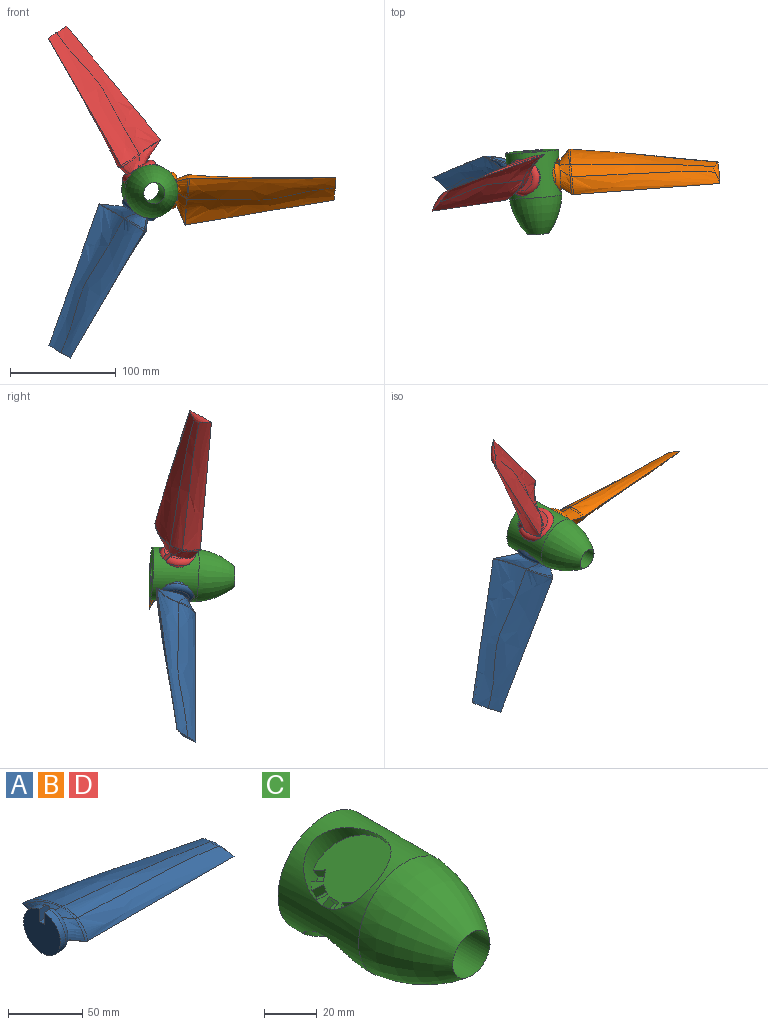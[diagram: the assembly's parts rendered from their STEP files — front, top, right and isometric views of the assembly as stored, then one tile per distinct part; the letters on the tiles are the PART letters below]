
ASSEMBLY  parts=4 mates=1
PART A: 31 faces, bbox 165.4x75.5x38.2 mm
  f0: plane 9.48x8.65mm, normal (1,0,0), area 28.5mm2, adj f11,f16,f21,f30
  f1: plane 22.9x10.19mm, normal (1,0,0), area 88.6mm2, adj f14,f15,f30
  f2: plane 9.2x7.84mm, normal (1,0,0), area 30.8mm2, adj f11,f12,f13,f20,f30
  f3: bspline ~140x50.01mm, area 3008.1mm2, adj f5,f6,f8,f10,f14,f23,f24,f27
  f4: bspline ~140x44.79mm, area 3177.1mm2, adj f5,f9,f10,f28,f29
  f5: bspline ~46.76x8.29mm, area 139.2mm2, adj f3,f4,f6,f7,f8,f9,f10
  f6: plane 3.68x0.3mm, normal (1,0,0), area 0.3mm2, adj f3,f5,f8
  f7: bspline ~140x14.27mm, area 2106.1mm2, adj f5,f8,f9,f25
  f8: bspline ~140x31.34mm, area 3409.3mm2, adj f3,f5,f6,f7,f24,f25
  f9: bspline ~134.76x13.88mm, area 1513.5mm2, adj f4,f5,f7,f25,f26
  f10: bspline ~146.74x35.65mm, area 378.7mm2, adj f3,f4,f5,f29
  f11: bspline ~16.56x9.38mm, area 97.8mm2, adj f0,f2,f12,f16,f19,f25,f26,f28
  f12: bspline ~36.99x15.08mm, area 217.7mm2, adj f2,f11,f13,f29
  f13: bspline ~30.31x12.09mm, area 57.8mm2, adj f2,f12,f14,f29,f30
  f14: bspline ~45.48x10.64mm, area 306.5mm2, adj f1,f3,f13,f15,f23,f24,f27,f29
  f15: bspline ~27.91x10.97mm, area 189.3mm2, adj f1,f14,f16,f24,f25,f30
  f16: bspline ~20.44x14.51mm, area 183.2mm2, adj f0,f11,f15,f25,f30
  f17: cylinder r=17.5mm len=35mm, axis (1,0,0), area 524.7mm2, adj f18,f20,f21,f30
  f18: plane 35x34.82mm, normal (-1,0,0), area 911.5mm2, adj f17,f20,f21,f22
  f19: plane 5x0.7mm, normal (-1,0,0), area 3mm2, adj f11,f20,f21,f22
  f20: plane 10.5x10.5mm, normal (0,-1,0), area 94.6mm2, adj f2,f17,f18,f19,f22,f30
  f21: plane 10.5x10.5mm, normal (0,1,0), area 94.6mm2, adj f0,f17,f18,f19,f22,f30
  f22: plane 10x5mm, normal (0,0,1), area 50mm2, adj f18,f19,f20,f21
  f23: bspline ~6.58x1.92mm, area 2.5mm2, adj f3,f14,f24
  f24: bspline ~28.34x3.32mm, area 39.4mm2, adj f3,f8,f14,f15,f23,f25
  f25: bspline ~15.48x11.23mm, area 36.8mm2, adj f7,f8,f9,f11,f15,f16,f24,f26
  f26: bspline ~14.26x3.07mm, area 21.6mm2, adj f9,f11,f25,f28
  f27: bspline ~28.01x2.7mm, area 15.1mm2, adj f3,f14,f29
  f28: bspline ~2.81x1.55mm, area 0.3mm2, adj f4,f11,f26,f29
  f29: bspline ~39.22x17.45mm, area 88mm2, adj f3,f4,f10,f11,f12,f13,f14,f27
  f30: torus R=12.5mm, axis (-1,0,0), area 704.3mm2, adj f0,f1,f2,f13,f14,f15,f16,f17
PART B: same geometry as A
PART C: 70 faces, bbox 52.7x78.6x60.8 mm
  f0: plane 35x30.16mm, normal (-0.5,0,0.87), area 832.3mm2, adj f8,f49,f50,f51,f53,f54,f55,f57
  f1: plane 35x30.16mm, normal (-0.5,0,-0.87), area 832.3mm2, adj f7,f29,f30,f31,f33,f34,f35,f37
  f2: plane 35x34.82mm, normal (1,0,0), area 832.3mm2, adj f6,f9,f10,f11,f13,f14,f15,f17
  f3: cylinder r=25mm len=50mm, axis (0,1,0), area 3675.1mm2, adj f4,f5,f6,f7,f8
  f4: revolved ~50x50mm, area 9429.9mm2, adj f3,f69
  f5: plane 50x50mm, normal (0,1,0), area 1649.3mm2, adj f3,f69
  f6: cylinder r=17.5mm len=35mm, axis (1,0,0), area 848.2mm2, adj f2,f3,f9,f11,f12,f13,f15,f16
  f7: cylinder r=17.5mm len=37.81mm, axis (-0.5,0,-0.87), area 848.2mm2, adj f1,f3,f29,f31,f32,f33,f35,f36
  f8: cylinder r=17.5mm len=37.81mm, axis (-0.5,0,0.87), area 848.5mm2, adj f0,f3,f49,f51,f52,f53,f55,f56
  f9: plane 5.07x5mm, normal (0,1,0), area 25.4mm2, adj f2,f6,f10,f12
  f10: plane 5x5mm, normal (0,0,1), area 25mm2, adj f2,f9,f11,f12
  f11: plane 5.07x5mm, normal (0,-1,0), area 25.4mm2, adj f2,f6,f10,f12
  f12: plane 5.25x5mm, normal (1,0,0), area 26mm2, adj f6,f9,f10,f11
  f13: plane 5x4.39mm, normal (0,0.5,0.87), area 25.4mm2, adj f2,f6,f14,f16
  f14: plane 5x4.33mm, normal (0,-0.87,0.5), area 25mm2, adj f2,f13,f15,f16
  f15: plane 5x4.39mm, normal (0,-0.5,-0.87), area 25.4mm2, adj f2,f6,f14,f16
  f16: plane 6.89x6.87mm, normal (1,0,0), area 26mm2, adj f6,f13,f14,f15
  f17: plane 5x4.39mm, normal (0,0.87,0.5), area 25.4mm2, adj f2,f6,f18,f20
  f18: plane 5x4.33mm, normal (0,-0.5,0.87), area 25mm2, adj f2,f17,f19,f20
  f19: plane 5x4.39mm, normal (0,-0.87,-0.5), area 25.4mm2, adj f2,f6,f18,f20
  f20: plane 6.89x6.87mm, normal (1,0,0), area 26mm2, adj f6,f17,f18,f19
  f21: plane 5x4.39mm, normal (0,0.5,-0.87), area 25.4mm2, adj f2,f6,f22,f24
  f22: plane 5x4.33mm, normal (0,0.87,0.5), area 25mm2, adj f2,f21,f23,f24
  f23: plane 5x4.39mm, normal (0,-0.5,0.87), area 25.4mm2, adj f2,f6,f22,f24
  f24: plane 6.89x6.87mm, normal (1,0,0), area 26mm2, adj f6,f21,f22,f23
  f25: plane 5x4.39mm, normal (0,0.87,-0.5), area 25.4mm2, adj f2,f6,f26,f28
  f26: plane 5x4.33mm, normal (0,0.5,0.87), area 25mm2, adj f2,f25,f27,f28
  f27: plane 5x4.39mm, normal (0,-0.87,0.5), area 25.4mm2, adj f2,f6,f26,f28
  f28: plane 6.89x6.87mm, normal (1,0,0), area 26mm2, adj f6,f25,f26,f27
  f29: plane 6.89x6.87mm, normal (0,1,0), area 25.4mm2, adj f1,f7,f30,f32
  f30: plane 5x4.33mm, normal (0.87,0,-0.5), area 25mm2, adj f1,f29,f31,f32
  f31: plane 6.89x6.87mm, normal (0,-1,0), area 25.4mm2, adj f1,f7,f30,f32
  f32: plane 5x4.55mm, normal (-0.5,0,-0.87), area 26mm2, adj f7,f29,f30,f31
  f33: plane 5.6x4.7mm, normal (0.75,0.5,-0.43), area 25.4mm2, adj f1,f7,f34,f36
  f34: plane 6.5x6.25mm, normal (0.43,-0.87,-0.25), area 25mm2, adj f1,f33,f35,f36
  f35: plane 5.6x4.7mm, normal (-0.75,-0.5,0.43), area 25.4mm2, adj f1,f7,f34,f36
  f36: plane 6.89x5.95mm, normal (-0.5,0,-0.87), area 26mm2, adj f7,f33,f34,f35
  f37: plane 6.53x6.3mm, normal (0.43,0.87,-0.25), area 25.4mm2, adj f1,f7,f38,f40
  f38: plane 5.58x4.67mm, normal (0.75,-0.5,-0.43), area 25mm2, adj f1,f37,f39,f40
  f39: plane 6.53x6.3mm, normal (-0.43,-0.87,0.25), area 25.4mm2, adj f1,f7,f38,f40
  f40: plane 6.87x5.97mm, normal (-0.5,0,-0.87), area 26mm2, adj f7,f37,f38,f39
  f41: plane 5.6x4.7mm, normal (-0.75,0.5,0.43), area 25.4mm2, adj f1,f7,f42,f44
  f42: plane 6.5x6.25mm, normal (0.43,0.87,-0.25), area 25mm2, adj f1,f41,f43,f44
  f43: plane 5.6x4.7mm, normal (0.75,-0.5,-0.43), area 25.4mm2, adj f1,f7,f42,f44
  f44: plane 6.89x5.95mm, normal (-0.5,0,-0.87), area 26mm2, adj f7,f41,f42,f43
  f45: plane 6.53x6.3mm, normal (-0.43,0.87,0.25), area 25.4mm2, adj f1,f7,f46,f48
  f46: plane 5.58x4.67mm, normal (0.75,0.5,-0.43), area 25mm2, adj f1,f45,f47,f48
  f47: plane 6.53x6.3mm, normal (0.43,-0.87,-0.25), area 25.4mm2, adj f1,f7,f46,f48
  f48: plane 6.87x5.97mm, normal (-0.5,0,-0.87), area 26mm2, adj f7,f45,f46,f47
  f49: plane 6.89x6.87mm, normal (0,1,0), area 25.4mm2, adj f0,f8,f50,f52
  f50: plane 5x4.33mm, normal (-0.87,0,-0.5), area 25mm2, adj f0,f49,f51,f52
  f51: plane 6.89x6.87mm, normal (0,-1,0), area 25.4mm2, adj f0,f8,f50,f52
  f52: plane 5x4.55mm, normal (-0.5,0,0.87), area 26mm2, adj f8,f49,f50,f51
  f53: plane 5.6x4.7mm, normal (-0.75,0.5,-0.43), area 25.4mm2, adj f0,f8,f54,f56
  f54: plane 6.5x6.25mm, normal (-0.43,-0.87,-0.25), area 25mm2, adj f0,f53,f55,f56
  f55: plane 5.6x4.7mm, normal (0.75,-0.5,0.43), area 25.4mm2, adj f0,f8,f54,f56
  f56: plane 6.89x5.95mm, normal (-0.5,0,0.87), area 26mm2, adj f8,f53,f54,f55
  f57: plane 6.53x6.3mm, normal (-0.43,0.87,-0.25), area 25.4mm2, adj f0,f8,f58,f60
  f58: plane 5.58x4.67mm, normal (-0.75,-0.5,-0.43), area 25mm2, adj f0,f57,f59,f60
  f59: plane 6.53x6.3mm, normal (0.43,-0.87,0.25), area 25.4mm2, adj f0,f8,f58,f60
  f60: plane 6.87x5.97mm, normal (-0.5,0,0.87), area 26mm2, adj f8,f57,f58,f59
  f61: plane 5.6x4.7mm, normal (0.75,0.5,0.43), area 25.4mm2, adj f0,f8,f62,f64
  f62: plane 6.5x6.25mm, normal (-0.43,0.87,-0.25), area 25mm2, adj f0,f61,f63,f64
  f63: plane 5.6x4.7mm, normal (-0.75,-0.5,-0.43), area 25.4mm2, adj f0,f8,f62,f64
  f64: plane 6.89x5.95mm, normal (-0.5,0,0.87), area 26mm2, adj f8,f61,f62,f63
  f65: plane 6.53x6.3mm, normal (0.43,0.87,0.25), area 25.4mm2, adj f0,f8,f66,f68
  f66: plane 5.58x4.67mm, normal (-0.75,0.5,-0.43), area 25mm2, adj f0,f65,f67,f68
  f67: plane 6.53x6.3mm, normal (-0.43,-0.87,-0.25), area 25.4mm2, adj f0,f8,f66,f68
  f68: plane 6.87x5.97mm, normal (-0.5,0,0.87), area 26mm2, adj f8,f65,f66,f67
  f69: cylinder r=10mm len=78.59mm, axis (0,1,0), area 4938mm2, adj f4,f5
PART D: same geometry as A
PLACE A rot(axis=(-0.25,0.86,0.44),127deg) t=(-59.43,-10.71,-23.52)mm
PLACE B rot(axis=(-1,-0.04,0.09),46.2deg) t=(-8.04,-8.23,8.6)mm
PLACE C rot(axis=(0.5,0,0.87),5deg) t=(-42.2,-20.66,6.94)mm fixed
PLACE D rot(axis=(-0.19,-0.9,-0.4),123.5deg) t=(-61.36,-13.51,37.04)mm
MATE revolute B.f17 <-> C.f6  axis (-1,-0.08,0) through (-28.74,0.32,7.83)mm
